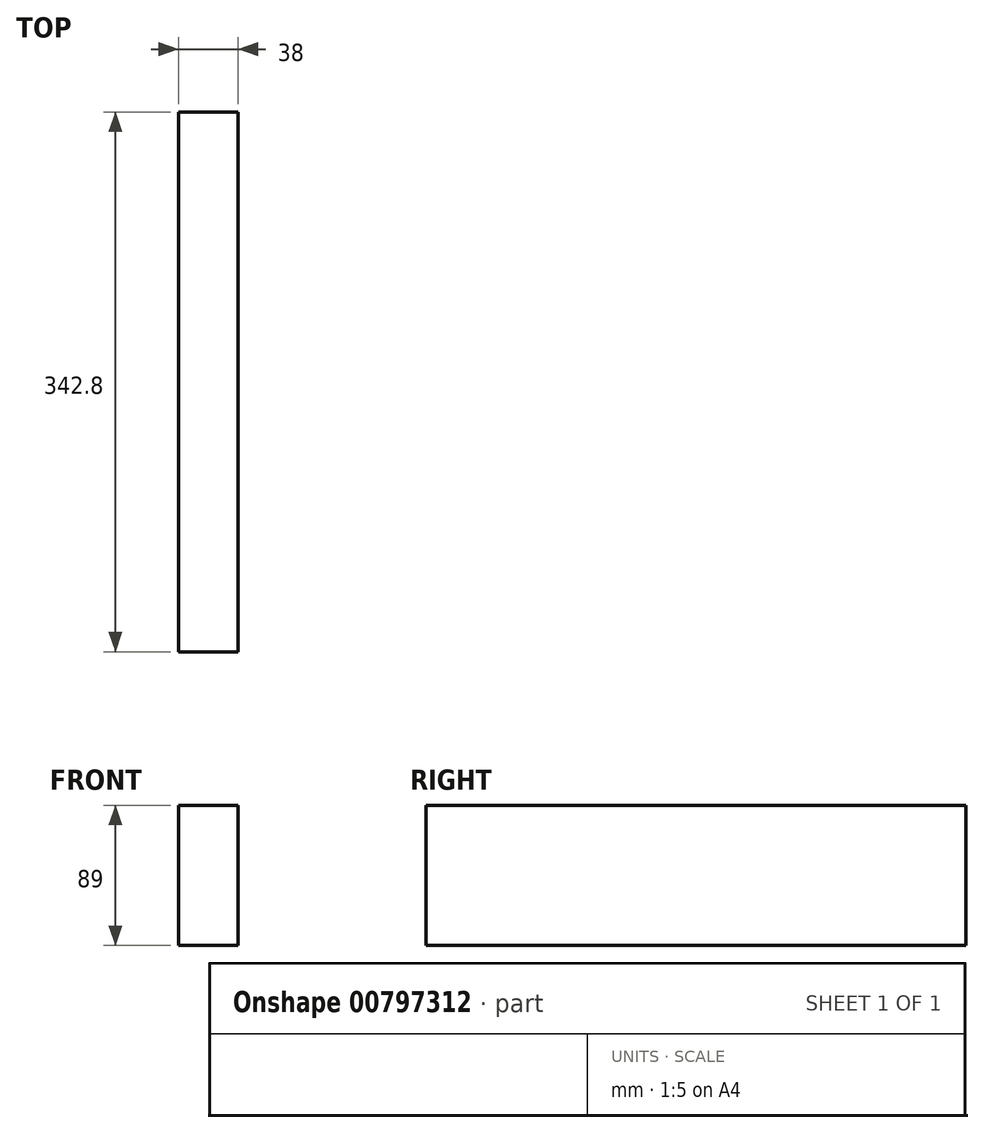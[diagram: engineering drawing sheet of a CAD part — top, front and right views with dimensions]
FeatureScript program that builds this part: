
annotation { "Feature Type Name" : "Feature", "Feature Type Description" : "" }
export const myFeature = defineFeature(function(context is Context, id is Id, definition is map)
    precondition{}
    {
        {
            var Q0;
            Q0=qCreatedBy(makeId("Front.planeOp"),FACE);
            var sketch = newSketch(context, id + "F0", { "sketchPlane" : qUnion([Q0])});
            skLineSegment(sketch, "E0.bottom", {"start": v(19, 44.5) * mm, "end": v(-19, 44.5) * mm});
            skLineSegment(sketch, "E0.top", {"start": v(19, -44.5) * mm, "end": v(-19, -44.5) * mm});
            skLineSegment(sketch, "E0.left", {"start": v(19, 44.5) * mm, "end": v(19, -44.5) * mm});
            skLineSegment(sketch, "E0.right", {"start": v(-19, 44.5) * mm, "end": v(-19, -44.5) * mm});
            skPoint(sketch, "E0.middle", {"position": v(0, 0) * mm});
            skSolve(sketch);
        }
        {
            var Q0;
            Q0 = qSketchRegion(id + "F0", true);
            extrude(context, id + "F1", {"entities" : qUnion([Q0]), "depth" : 342.8 * mm, "offsetDistance" : 25 * mm, "symmetric" : true});
        }
    });
